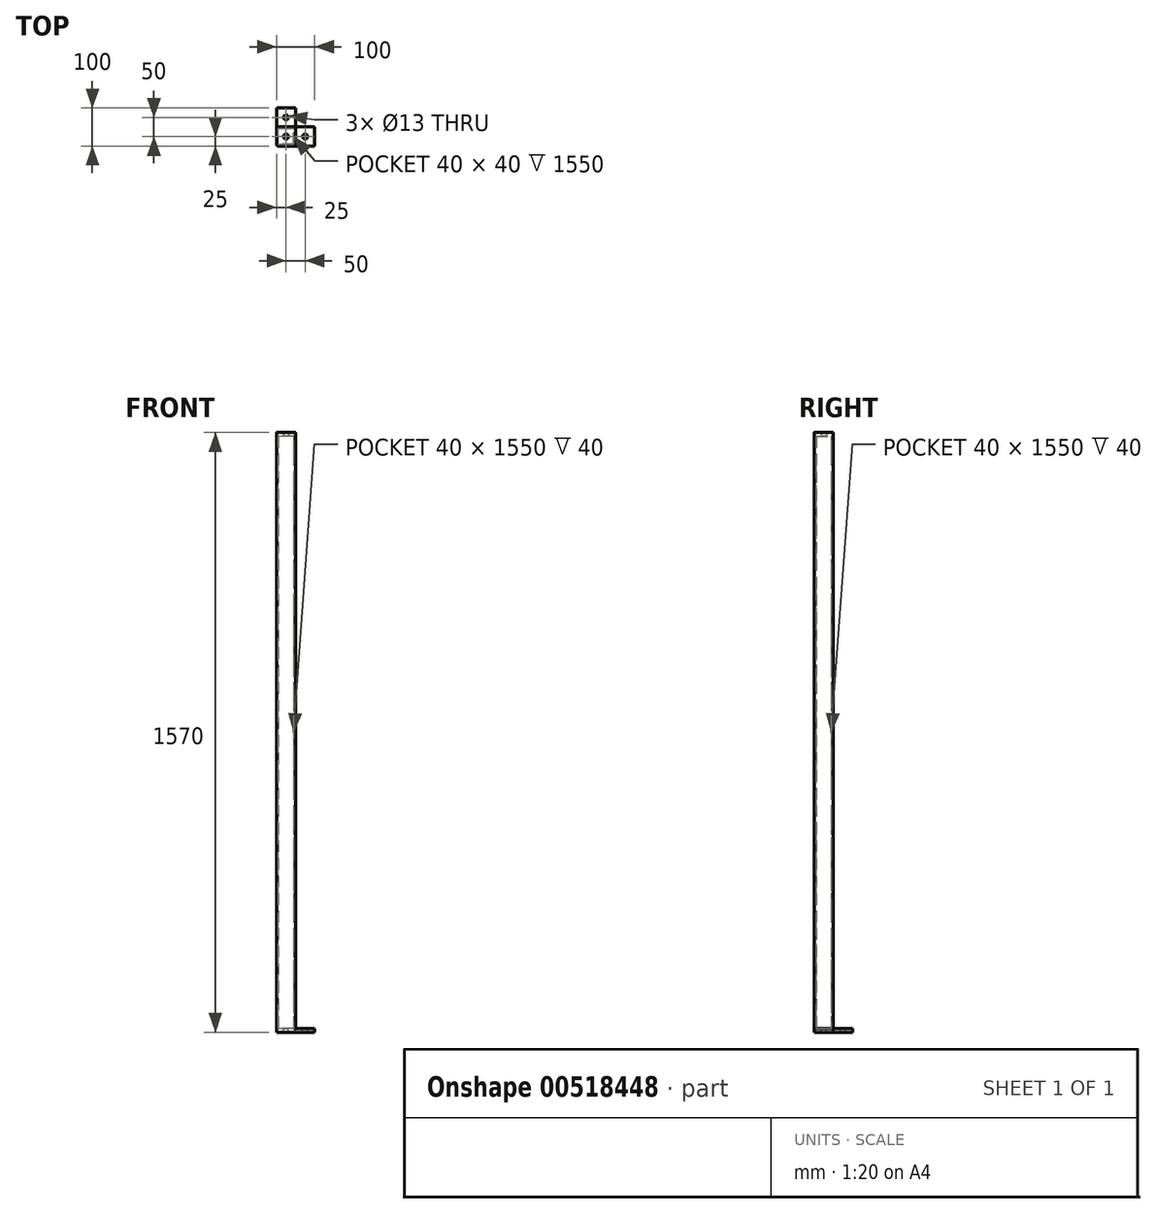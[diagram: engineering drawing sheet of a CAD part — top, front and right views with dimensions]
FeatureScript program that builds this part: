
annotation { "Feature Type Name" : "Feature", "Feature Type Description" : "" }
export const myFeature = defineFeature(function(context is Context, id is Id, definition is map)
    precondition{}
    {
        {
            var Q0;
            Q0=qCreatedBy(makeId("Top.planeOp"),FACE);
            var sketch = newSketch(context, id + "F0", { "sketchPlane" : qUnion([Q0])});
            skLineSegment(sketch, "E0.bottom", {"start": v(20, -25) * mm, "end": v(-20, -25) * mm});
            skLineSegment(sketch, "E0.top", {"start": v(20, 25) * mm, "end": v(-20, 25) * mm});
            skLineSegment(sketch, "E0.left", {"start": v(25, -20) * mm, "end": v(25, 20) * mm});
            skLineSegment(sketch, "E0.right", {"start": v(-25, -20) * mm, "end": v(-25, 20) * mm});
            skPoint(sketch, "E0.middle", {"position": v(0, 0) * mm});
            skLineSegment(sketch, "E1.bottom", {"start": v(20, -20) * mm, "end": v(-20, -20) * mm});
            skLineSegment(sketch, "E1.top", {"start": v(20, 20) * mm, "end": v(-20, 20) * mm});
            skLineSegment(sketch, "E1.left", {"start": v(20, -20) * mm, "end": v(20, 20) * mm});
            skLineSegment(sketch, "E1.right", {"start": v(-20, -20) * mm, "end": v(-20, 20) * mm});
            skPoint(sketch, "E2.visualSharp", {"position": v(-25, 25) * mm});
            skArc(sketch, "E2.filletArc", {"start": v(-20, 25) * mm, "mid": v(-23.54, 23.54) * mm, "end": v(-25, 20) * mm});
            skPoint(sketch, "E3.visualSharp", {"position": v(25, 25) * mm});
            skArc(sketch, "E3.filletArc", {"start": v(25, 20) * mm, "mid": v(23.54, 23.54) * mm, "end": v(20, 25) * mm});
            skPoint(sketch, "E4.visualSharp", {"position": v(-25, -25) * mm});
            skArc(sketch, "E4.filletArc", {"start": v(-25, -20) * mm, "mid": v(-23.54, -23.54) * mm, "end": v(-20, -25) * mm});
            skPoint(sketch, "E5.visualSharp", {"position": v(25, -25) * mm});
            skArc(sketch, "E5.filletArc", {"start": v(20, -25) * mm, "mid": v(23.54, -23.54) * mm, "end": v(25, -20) * mm});
            skSolve(sketch);
        }
        {
            var Q0;
            Q0=qSketchRegion(id+"F0",true);
            extrude(context, id + "F1", {"entities" : qUnion([Q0]), "depth" : 1550 * mm, "offsetDistance" : 25 * mm});
        }
        {
            var Q0;
            Q0=makeQuery(id+"F1.opExtrude","CAP_FACE",FACE,{"disambiguationData":[OSD([sQuery(id+"F0.wireOp",EDGE,"E0.bottom"),sQuery(id+"F0.wireOp",EDGE,"E0.top"),sQuery(id+"F0.wireOp",EDGE,"E0.left"),sQuery(id+"F0.wireOp",EDGE,"E0.right"),sQuery(id+"F0.wireOp",EDGE,"E1.bottom"),sQuery(id+"F0.wireOp",EDGE,"E1.top"),sQuery(id+"F0.wireOp",EDGE,"E1.left"),sQuery(id+"F0.wireOp",EDGE,"E1.right"),sQuery(id+"F0.wireOp",EDGE,"E2.filletArc"),sQuery(id+"F0.wireOp",EDGE,"E3.filletArc"),sQuery(id+"F0.wireOp",EDGE,"E4.filletArc"),sQuery(id+"F0.wireOp",EDGE,"E5.filletArc")])],"isStart":false});
            var sketch = newSketch(context, id + "F2", { "sketchPlane" : qUnion([Q0])});
            skArc(sketch, "E6.0", {"start": v(-20, 25) * mm, "mid": v(-23.54, 23.54) * mm, "end": v(-25, 20) * mm});
            skArc(sketch, "E6.1", {"start": v(25, 20) * mm, "mid": v(23.54, 23.54) * mm, "end": v(20, 25) * mm});
            skArc(sketch, "E6.2", {"start": v(20, -25) * mm, "mid": v(23.54, -23.54) * mm, "end": v(25, -20) * mm});
            skArc(sketch, "E7.0", {"start": v(-25, -20) * mm, "mid": v(-23.54, -23.54) * mm, "end": v(-20, -25) * mm});
            skLineSegment(sketch, "E8.0", {"start": v(-25, -20) * mm, "end": v(-25, 20) * mm});
            skLineSegment(sketch, "E9.0", {"start": v(-20, -20) * mm, "end": v(-20, 20) * mm});
            skLineSegment(sketch, "E10.0", {"start": v(20, 20) * mm, "end": v(-20, 20) * mm});
            skLineSegment(sketch, "E11.0", {"start": v(20, 25) * mm, "end": v(-20, 25) * mm});
            skLineSegment(sketch, "E12.0", {"start": v(25, -20) * mm, "end": v(25, 20) * mm});
            skLineSegment(sketch, "E13.0", {"start": v(20, -25) * mm, "end": v(-20, -25) * mm});
            skCircle(sketch, "E14", {"center": v(0, 0) * mm, "radius": 6.5 * mm});
            skSolve(sketch);
        }
        {
            var Q0;
            Q0 = qSketchRegion(id + "F2", true);
            extrude(context, id + "F3", {"entities" : qUnion([Q0]), "operationType" : NewBodyOperationType.ADD, "depth" : 10 * mm, "offsetDistance" : 25 * mm});
        }
        {
            var Q0;
            Q0=makeQuery(id+"F1.opExtrude","CAP_FACE",FACE,{"disambiguationData":[OSD([sQuery(id+"F0.wireOp",EDGE,"E0.bottom"),sQuery(id+"F0.wireOp",EDGE,"E0.top"),sQuery(id+"F0.wireOp",EDGE,"E0.left"),sQuery(id+"F0.wireOp",EDGE,"E0.right"),sQuery(id+"F0.wireOp",EDGE,"E1.bottom"),sQuery(id+"F0.wireOp",EDGE,"E1.top"),sQuery(id+"F0.wireOp",EDGE,"E1.left"),sQuery(id+"F0.wireOp",EDGE,"E1.right"),sQuery(id+"F0.wireOp",EDGE,"E2.filletArc"),sQuery(id+"F0.wireOp",EDGE,"E3.filletArc"),sQuery(id+"F0.wireOp",EDGE,"E4.filletArc"),sQuery(id+"F0.wireOp",EDGE,"E5.filletArc")])],"isStart":true});
            var sketch = newSketch(context, id + "F4", { "sketchPlane" : qUnion([Q0])});
            skArc(sketch, "E15.1", {"start": v(-25, 20) * mm, "mid": v(-23.54, 23.54) * mm, "end": v(-20, 25) * mm});
            skLineSegment(sketch, "E16", {"start": v(-20, 25) * mm, "end": v(75, 25) * mm});
            skLineSegment(sketch, "E17", {"start": v(75, 25) * mm, "end": v(75, -25) * mm});
            skLineSegment(sketch, "E18", {"start": v(75, -25) * mm, "end": v(25, -25) * mm});
            skLineSegment(sketch, "E19", {"start": v(25, -25) * mm, "end": v(25, -75) * mm});
            skLineSegment(sketch, "E20", {"start": v(25, -75) * mm, "end": v(-25, -75) * mm});
            skLineSegment(sketch, "E21", {"start": v(-25, -75) * mm, "end": v(-25, 20) * mm});
            skCircle(sketch, "E22", {"center": v(50, 0) * mm, "radius": 6.5 * mm});
            skCircle(sketch, "E23", {"center": v(0, -50) * mm, "radius": 6.5 * mm});
            skPoint(sketch, "E23.centerSnap0", {"position": v(0, -20) * mm});
            skSolve(sketch);
        }
        {
            var Q0;
            Q0 = qSketchRegion(id + "F4", true);
            extrude(context, id + "F5", {"entities" : qUnion([Q0]), "operationType" : NewBodyOperationType.ADD, "depth" : 10 * mm, "offsetDistance" : 25 * mm});
        }
    });
